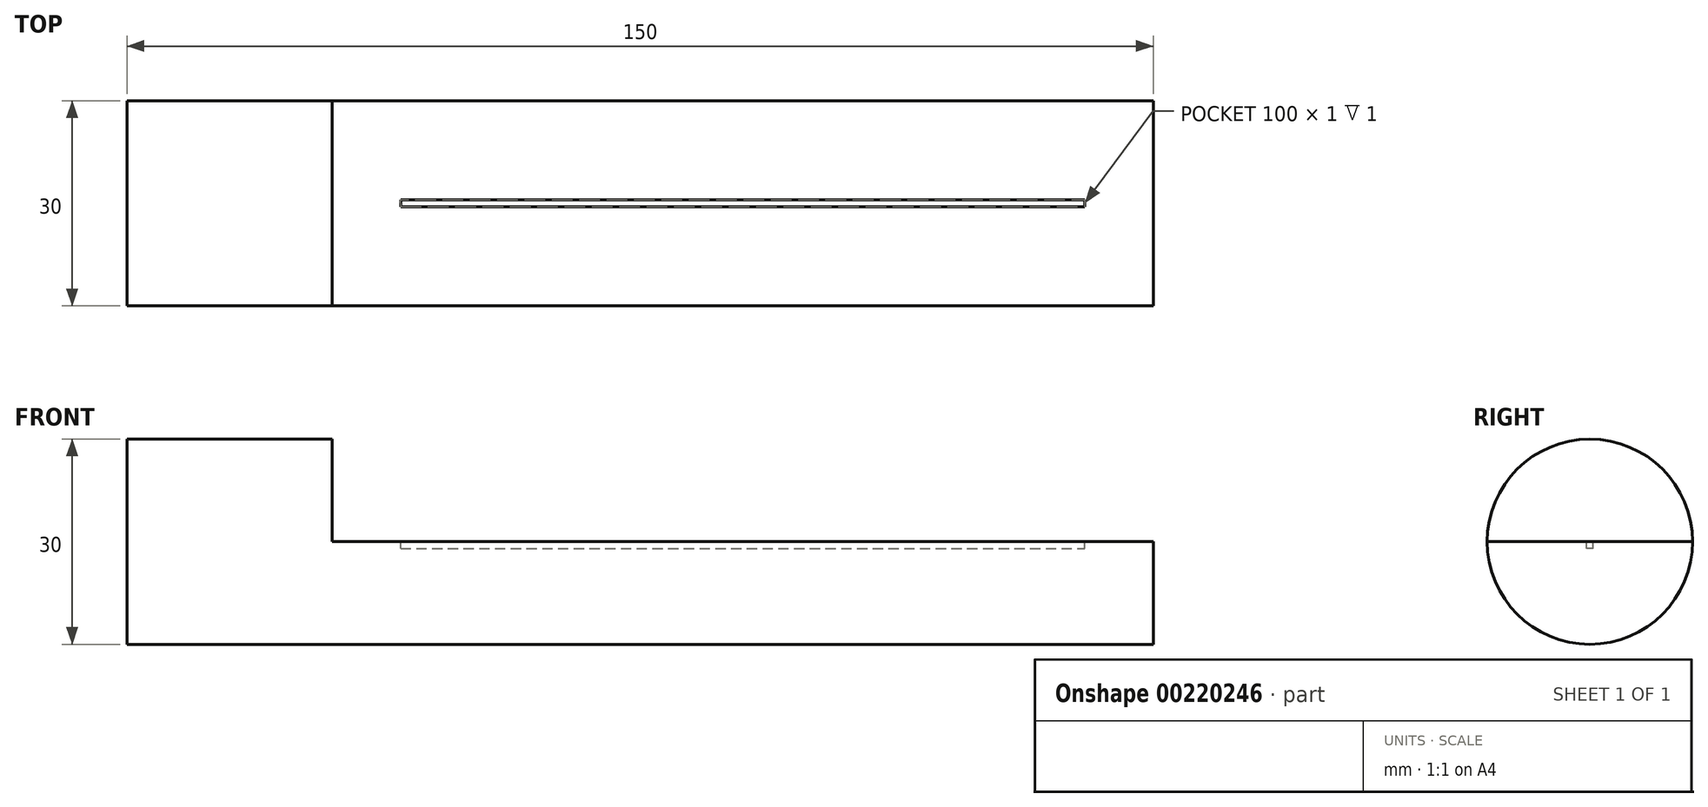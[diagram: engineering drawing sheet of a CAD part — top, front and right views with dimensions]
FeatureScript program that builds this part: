
annotation { "Feature Type Name" : "Feature", "Feature Type Description" : "" }
export const myFeature = defineFeature(function(context is Context, id is Id, definition is map)
    precondition{}
    {
        {
            var Q0;
            Q0=qCreatedBy(makeId("Right.planeOp"),FACE);
            var sketch = newSketch(context, id + "F0", { "sketchPlane" : qUnion([Q0])});
            skCircle(sketch, "E0", {"center": v(0, 0) * mm, "radius": 15 * mm});
            skSolve(sketch);
        }
        {
            var Q0;
            Q0 = qSketchRegion(id + "F0", true);
            extrude(context, id + "F1", {"entities" : qUnion([Q0]), "depth" : 150 * mm, "offsetDistance" : 25 * mm});
        }
        {
            var Q0;
            Q0=makeQuery(id+"F1.opExtrude","CAP_FACE",FACE,{"disambiguationData":[OSD([sQuery(id+"F0.wireOp",EDGE,"E0")])],"isStart":false});
            var sketch = newSketch(context, id + "F2", { "sketchPlane" : qUnion([Q0])});
            skLineSegment(sketch, "E1", {"start": v(-15, 0) * mm, "end": v(15, 0) * mm});
            skSolve(sketch);
        }
        {
            var Q0;
            Q0 = qSketchRegion(id + "F2", true);
            var Q1;
            {var subQ0=sQuery(id+"F2.wireOp",EDGE,"E1");Q1=makeQuery(id+"F2.imprint","IMPRINT",FACE,{"disambiguationData":[TD([[makeQuery(id+"F2.imprint","IMPRINT",EDGE,{"derivedFrom":subQ0}),1.0]])]});}
            extrude(context, id + "F3", {"entities" : qUnion([Q0, Q1]), "operationType" : NewBodyOperationType.REMOVE, "oppositeDirection" : true, "depth" : 120 * mm, "offsetDistance" : 25 * mm});
        }
        {
            var Q0;
            Q0=makeQuery(id+"F3.boolean.opBoolean","COPY",FACE,{"derivedFrom":makeQuery(id+"F3.opExtrude","SWEPT_FACE",FACE,{"disambiguationData":[OSD([sQuery(id+"F2.wireOp",EDGE,"E1")])]})});
            var sketch = newSketch(context, id + "F4", { "sketchPlane" : qUnion([Q0])});
            skLineSegment(sketch, "E2.0", {"start": v(140, -15) * mm, "end": v(140, 15) * mm, "construction": true});
            skLineSegment(sketch, "E3.0", {"start": v(40, 15) * mm, "end": v(40, -15) * mm, "construction": true});
            skLineSegment(sketch, "E4.0", {"start": v(40, -0.5) * mm, "end": v(140, -0.5) * mm});
            skLineSegment(sketch, "E5.0", {"start": v(155, -20) * mm, "end": v(155, 20) * mm});
            skLineSegment(sketch, "E5.1", {"start": v(25, -20) * mm, "end": v(155, -20) * mm});
            skLineSegment(sketch, "E5.2", {"start": v(25, 20) * mm, "end": v(25, -20) * mm});
            skLineSegment(sketch, "E5.3", {"start": v(155, 20) * mm, "end": v(25, 20) * mm});
            skLineSegment(sketch, "E6.0", {"start": v(40, 0.5) * mm, "end": v(140, 0.5) * mm});
            skLineSegment(sketch, "E7", {"start": v(140, 0.5) * mm, "end": v(140, -0.5) * mm});
            skLineSegment(sketch, "E8", {"start": v(40, -0.5) * mm, "end": v(40, 0.5) * mm});
            skSolve(sketch);
        }
        {
            var Q0;
            Q0=makeQuery(id+"F4.imprint","IMPRINT",FACE,{"disambiguationData":[TD([[makeQuery(id+"F4.imprint","IMPRINT",EDGE,{"derivedFrom":sQuery(id+"F4.wireOp",EDGE,"E4.0")}),1.0]])]});
            extrude(context, id + "F5", {"entities" : qUnion([Q0]), "operationType" : NewBodyOperationType.REMOVE, "oppositeDirection" : true, "depth" : 1 * mm, "offsetDistance" : 25 * mm});
        }
    });
